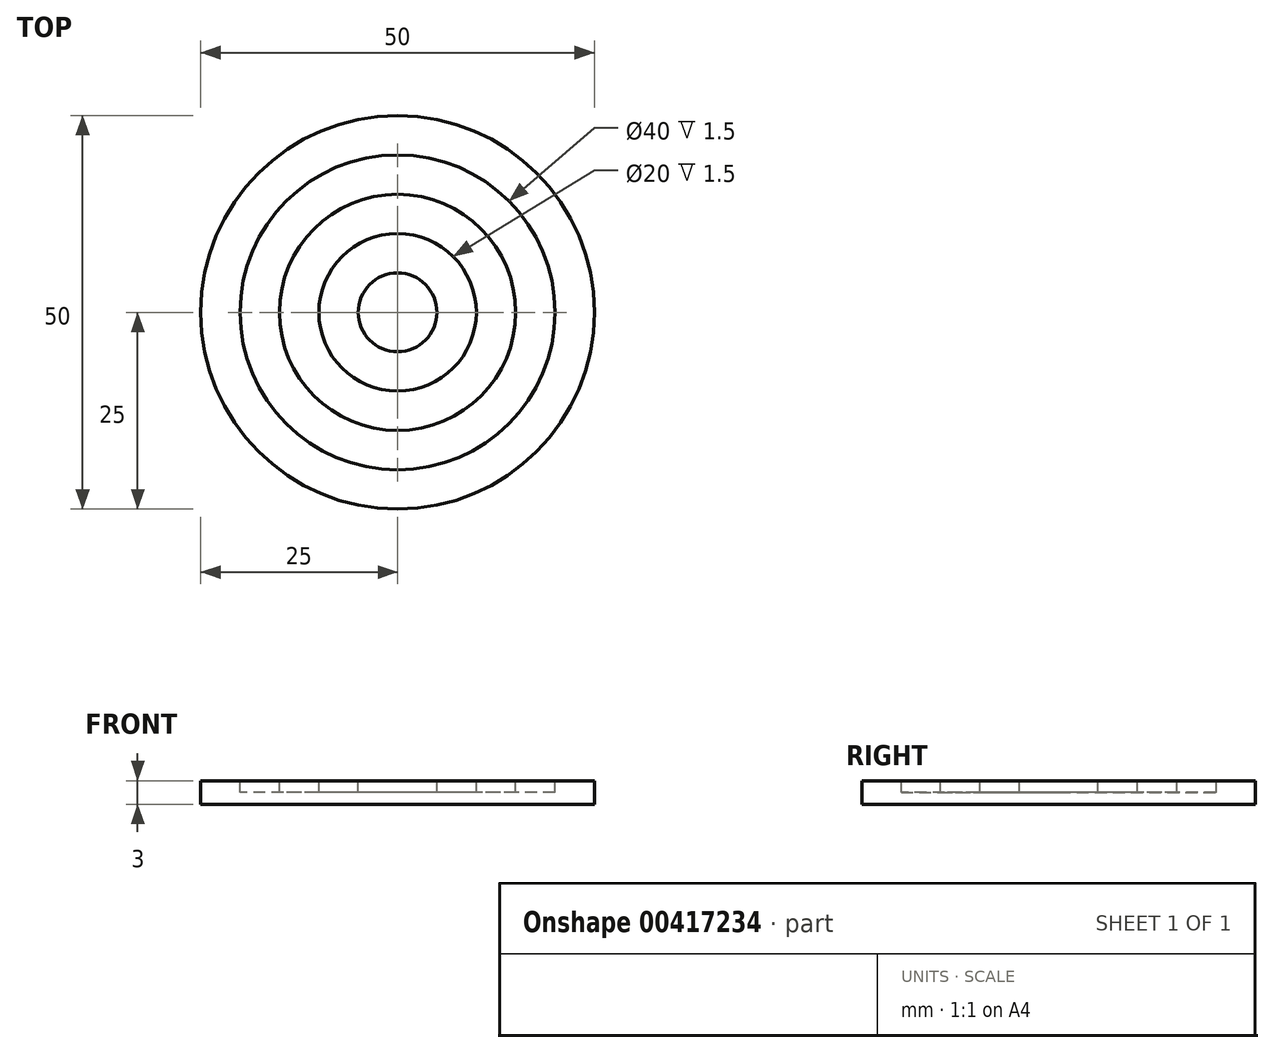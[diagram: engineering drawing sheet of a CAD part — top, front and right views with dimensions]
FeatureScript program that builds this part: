
annotation { "Feature Type Name" : "Feature", "Feature Type Description" : "" }
export const myFeature = defineFeature(function(context is Context, id is Id, definition is map)
    precondition{}
    {
        {
            var Q0;
            Q0=qCreatedBy(makeId("Top.planeOp"),FACE);
            var sketch = newSketch(context, id + "F0", { "sketchPlane" : qUnion([Q0])});
            skCircle(sketch, "E0", {"center": v(0, 0) * mm, "radius": 25 * mm});
            skSolve(sketch);
        }
        {
            var Q0;
            Q0 = qSketchRegion(id + "F0", true);
            extrude(context, id + "F1", {"entities" : qUnion([Q0]), "depth" : 3 * mm});
        }
        {
            var Q0;
            Q0=makeQuery(id+"F1.opExtrude","CAP_FACE",FACE,{"disambiguationData":[OSD([sQuery(id+"F0.wireOp",EDGE,"E0")])],"isStart":false});
            var sketch = newSketch(context, id + "F2", { "sketchPlane" : qUnion([Q0])});
            skCircle(sketch, "E1", {"center": v(0, 0) * mm, "radius": 5 * mm});
            skCircle(sketch, "E2", {"center": v(0, 0) * mm, "radius": 10 * mm});
            skCircle(sketch, "E3", {"center": v(0, 0) * mm, "radius": 15 * mm});
            skCircle(sketch, "E4", {"center": v(0, 0) * mm, "radius": 20 * mm});
            skSolve(sketch);
        }
        {
            var Q0;
            Q0 = qSketchRegion(id + "F2", true);
            var Q1;
            Q1=makeQuery(id+"F2.imprint","IMPRINT",FACE,{"disambiguationData":[TD([[makeQuery(id+"F2.imprint","IMPRINT",EDGE,{"derivedFrom":sQuery(id+"F2.wireOp",EDGE,"E1")}),-1.0]])]});
            extrude(context, id + "F3", {"entities" : qUnion([Q0, Q1]), "operationType" : NewBodyOperationType.REMOVE, "oppositeDirection" : true, "depth" : 1.5 * mm});
        }
    });
